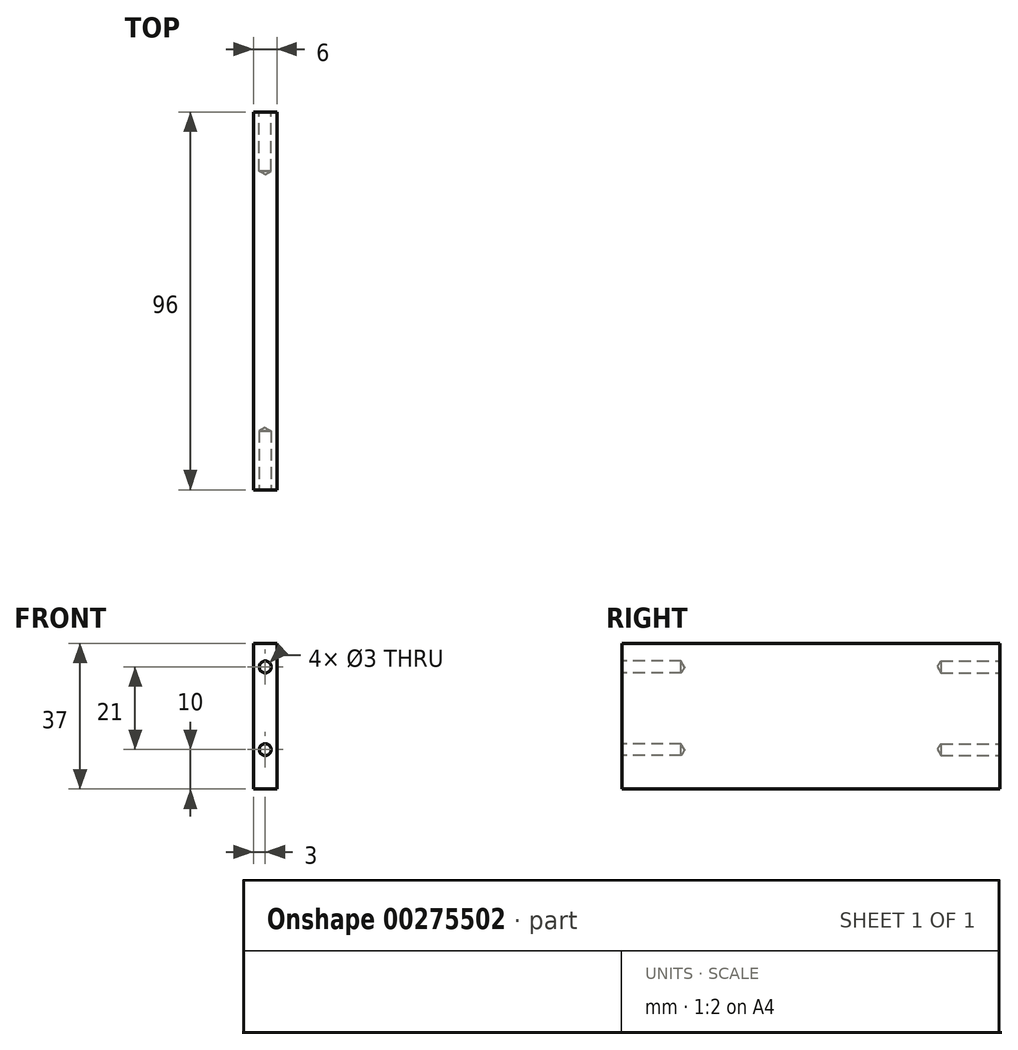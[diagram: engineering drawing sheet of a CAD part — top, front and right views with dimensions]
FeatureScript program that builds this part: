
annotation { "Feature Type Name" : "Feature", "Feature Type Description" : "" }
export const myFeature = defineFeature(function(context is Context, id is Id, definition is map)
    precondition{}
    {
        {
            var Q0;
            Q0=qCreatedBy(makeId("Top.planeOp"),FACE);
            var sketch = newSketch(context, id + "F0", { "sketchPlane" : qUnion([Q0])});
            skLineSegment(sketch, "E0.bottom", {"start": v(0, 0) * mm, "end": v(6, 0) * mm});
            skLineSegment(sketch, "E0.top", {"start": v(0, 96) * mm, "end": v(6, 96) * mm});
            skLineSegment(sketch, "E0.left", {"start": v(0, 0) * mm, "end": v(0, 96) * mm});
            skLineSegment(sketch, "E0.right", {"start": v(6, 0) * mm, "end": v(6, 96) * mm});
            skSolve(sketch);
        }
        {
            var Q0;
            Q0=makeQuery(id+"F0.imprint","IMPRINT",FACE,{"disambiguationData":[TD([[makeQuery(id+"F0.imprint","IMPRINT",EDGE,{"derivedFrom":sQuery(id+"F0.wireOp",EDGE,"E0.bottom")}),1.0]])]});
            extrude(context, id + "F1", {"entities" : qUnion([Q0]), "depth" : 37 * mm});
        }
        {
            var Q0;
            Q0=makeQuery(id+"F1.opExtrude","SWEPT_FACE",FACE,{"disambiguationData":[OSD([sQuery(id+"F0.wireOp",EDGE,"E0.bottom")])]});
            var sketch = newSketch(context, id + "F2", { "sketchPlane" : qUnion([Q0])});
            skPoint(sketch, "E1", {"position": v(10, 18.5) * mm});
            skPoint(sketch, "E1.positionSnap0", {"position": v(0, 18.5) * mm});
            skPoint(sketch, "E2", {"position": v(-4, 18.5) * mm});
            skPoint(sketch, "E2.positionSnap0", {"position": v(6, 18.5) * mm});
            skPoint(sketch, "E3", {"position": v(-116.5, 18.5) * mm});
            skSolve(sketch);
        }
        {
            var Q0;
            Q0=sQuery(id+"F2.wireOp",VERTEX,"E1");
            var Q1;
            Q1=sQuery(id+"F2.wireOp",VERTEX,"E3");
            var Q2;
            Q2=sQuery(id+"F2.wireOp",VERTEX,"E2");
            var Q3;
            Q3=makeQuery(id+"F1.opExtrude","SWEPT_BODY",BODY,{"disambiguationData":[OSD([sQuery(id+"F0.wireOp",EDGE,"E0.bottom"),sQuery(id+"F0.wireOp",EDGE,"E0.top"),sQuery(id+"F0.wireOp",EDGE,"E0.left"),sQuery(id+"F0.wireOp",EDGE,"E0.right")])]});
            hole(context, id + "F3", {"style" : HoleStyle.SIMPLE, "endStyle" : HoleEndStyle.BLIND, "holeDiameter" : 3 * mm, "holeDepth" : 20 * mm, "tappedDepth" : 12 * mm, "tapClearance" : 3, "locations" : qUnion([Q0, Q1, Q2]), "scope" : qUnion([Q3])});
        }
        {
            var Q0;
            Q0=makeQuery(id+"F1.opExtrude","SWEPT_FACE",FACE,{"disambiguationData":[OSD([sQuery(id+"F0.wireOp",EDGE,"E0.top")])]});
            var sketch = newSketch(context, id + "F4", { "sketchPlane" : qUnion([Q0])});
            skPoint(sketch, "E4", {"position": v(4, 18.5) * mm});
            skPoint(sketch, "E4.positionSnap0", {"position": v(-6, 18.5) * mm});
            skPoint(sketch, "E5", {"position": v(-10, 18.5) * mm});
            skPoint(sketch, "E5.positionSnap0", {"position": v(0, 18.5) * mm});
            skPoint(sketch, "E6", {"position": v(-122.5, 18.5) * mm});
            skSolve(sketch);
        }
        {
            var Q0;
            Q0=sQuery(id+"F4.wireOp",VERTEX,"E4");
            var Q1;
            Q1=sQuery(id+"F4.wireOp",VERTEX,"E6");
            var Q2;
            Q2=sQuery(id+"F4.wireOp",VERTEX,"E5");
            var Q3;
            Q3=makeQuery(id+"F1.opExtrude","SWEPT_BODY",BODY,{"disambiguationData":[OSD([sQuery(id+"F0.wireOp",EDGE,"E0.bottom"),sQuery(id+"F0.wireOp",EDGE,"E0.top"),sQuery(id+"F0.wireOp",EDGE,"E0.left"),sQuery(id+"F0.wireOp",EDGE,"E0.right")])]});
            hole(context, id + "F5", {"style" : HoleStyle.SIMPLE, "endStyle" : HoleEndStyle.BLIND, "holeDiameter" : 3 * mm, "holeDepth" : 20 * mm, "tappedDepth" : 12 * mm, "tapClearance" : 3, "locations" : qUnion([Q0, Q1, Q2]), "scope" : qUnion([Q3])});
        }
        {
            var Q0;
            Q0=makeQuery(id+"F1.opExtrude","SWEPT_FACE",FACE,{"disambiguationData":[OSD([sQuery(id+"F0.wireOp",EDGE,"E0.bottom")])]});
            var sketch = newSketch(context, id + "F6", { "sketchPlane" : qUnion([Q0])});
            skPoint(sketch, "E7", {"position": v(3, 31) * mm});
            skPoint(sketch, "E7.positionSnap0", {"position": v(3, 37) * mm});
            skPoint(sketch, "E8", {"position": v(3, 10) * mm});
            skPoint(sketch, "E8.positionSnap0", {"position": v(3, 0) * mm});
            skSolve(sketch);
        }
        {
            var Q0;
            Q0=sQuery(id+"F6.wireOp",VERTEX,"E7");
            var Q1;
            Q1=sQuery(id+"F6.wireOp",VERTEX,"E8");
            var Q2;
            Q2=makeQuery(id+"F1.opExtrude","SWEPT_BODY",BODY,{"disambiguationData":[OSD([sQuery(id+"F0.wireOp",EDGE,"E0.bottom"),sQuery(id+"F0.wireOp",EDGE,"E0.top"),sQuery(id+"F0.wireOp",EDGE,"E0.left"),sQuery(id+"F0.wireOp",EDGE,"E0.right")])]});
            hole(context, id + "F7", {"style" : HoleStyle.SIMPLE, "endStyle" : HoleEndStyle.BLIND, "holeDiameter" : 3 * mm, "holeDepth" : 15 * mm, "tappedDepth" : 12 * mm, "tapClearance" : 3, "locations" : qUnion([Q0, Q1]), "scope" : qUnion([Q2])});
        }
        {
            var Q0;
            Q0=makeQuery(id+"F1.opExtrude","SWEPT_FACE",FACE,{"disambiguationData":[OSD([sQuery(id+"F0.wireOp",EDGE,"E0.top")])]});
            var sketch = newSketch(context, id + "F8", { "sketchPlane" : qUnion([Q0])});
            skPoint(sketch, "E9", {"position": v(-3, 31) * mm});
            skPoint(sketch, "E9.positionSnap0", {"position": v(-3, 37) * mm});
            skPoint(sketch, "E10", {"position": v(-3, 10) * mm});
            skPoint(sketch, "E10.positionSnap0", {"position": v(-3, 0) * mm});
            skSolve(sketch);
        }
        {
            var Q0;
            Q0=sQuery(id+"F8.wireOp",VERTEX,"E10");
            var Q1;
            Q1=sQuery(id+"F8.wireOp",VERTEX,"E9");
            var Q2;
            Q2=makeQuery(id+"F1.opExtrude","SWEPT_BODY",BODY,{"disambiguationData":[OSD([sQuery(id+"F0.wireOp",EDGE,"E0.bottom"),sQuery(id+"F0.wireOp",EDGE,"E0.top"),sQuery(id+"F0.wireOp",EDGE,"E0.left"),sQuery(id+"F0.wireOp",EDGE,"E0.right")])]});
            hole(context, id + "F9", {"style" : HoleStyle.SIMPLE, "endStyle" : HoleEndStyle.BLIND, "holeDiameter" : 3 * mm, "holeDepth" : 15 * mm, "tappedDepth" : 12 * mm, "tapClearance" : 3, "locations" : qUnion([Q0, Q1]), "scope" : qUnion([Q2])});
        }
    });
